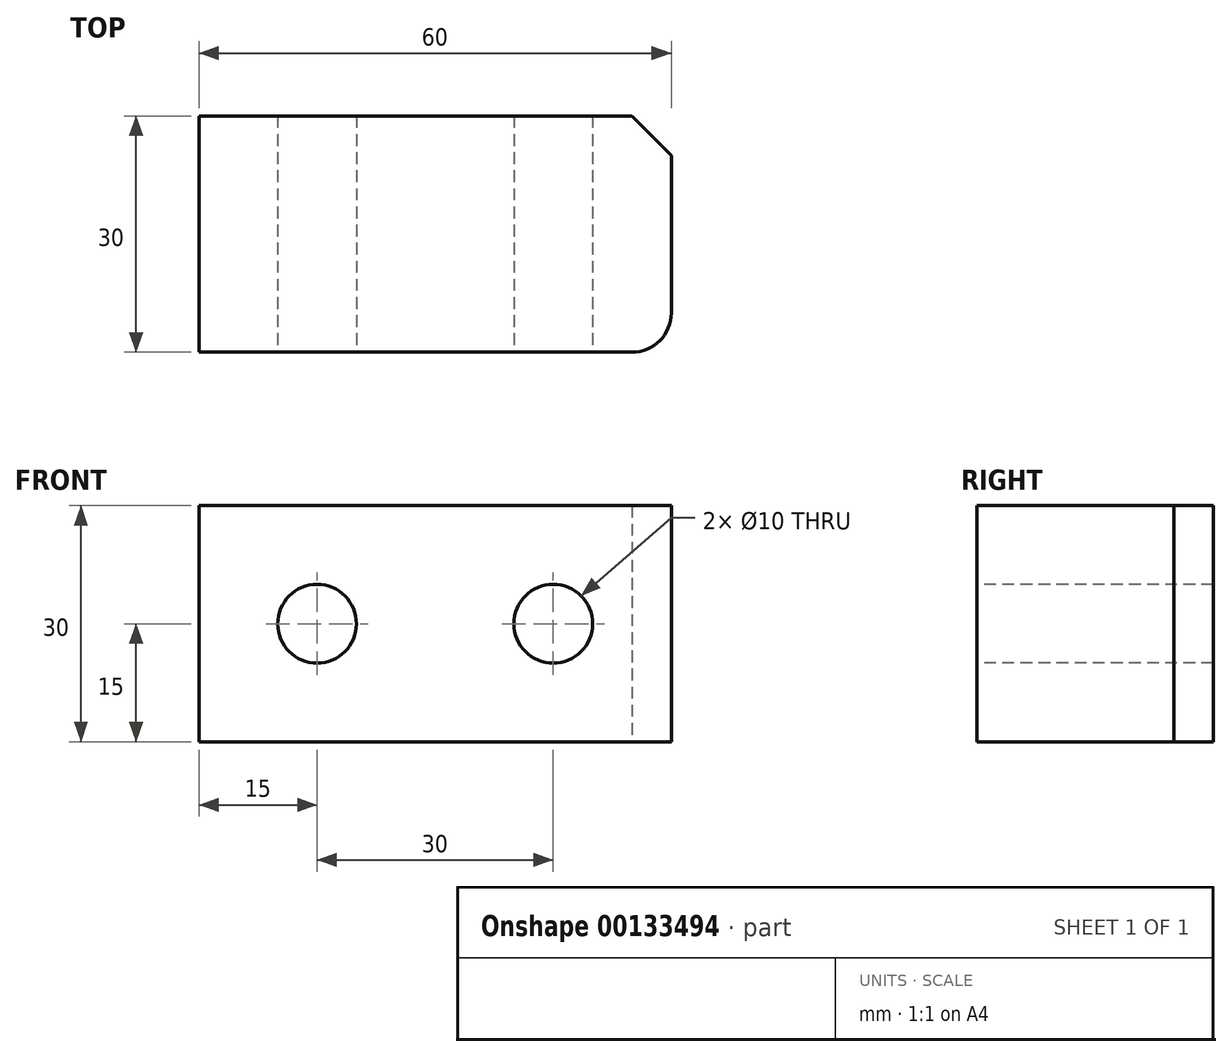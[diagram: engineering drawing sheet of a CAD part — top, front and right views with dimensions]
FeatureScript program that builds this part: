
annotation { "Feature Type Name" : "Feature", "Feature Type Description" : "" }
export const myFeature = defineFeature(function(context is Context, id is Id, definition is map)
    precondition{}
    {
        {
            var Q0;
            Q0=qCreatedBy(makeId("Top.planeOp"),FACE);
            var sketch = newSketch(context, id + "F0", { "sketchPlane" : qUnion([Q0])});
            skLineSegment(sketch, "E0.bottom", {"start": v(-15, 15) * mm, "end": v(15, 15) * mm});
            skLineSegment(sketch, "E0.top", {"start": v(-15, -15) * mm, "end": v(15, -15) * mm});
            skLineSegment(sketch, "E0.left", {"start": v(-15, 15) * mm, "end": v(-15, -15) * mm});
            skLineSegment(sketch, "E0.right", {"start": v(15, 15) * mm, "end": v(15, -15) * mm});
            skPoint(sketch, "E0.middle", {"position": v(0, 0) * mm});
            skSolve(sketch);
        }
        {
            var Q0;
            Q0 = qSketchRegion(id + "F0", true);
            extrude(context, id + "F1", {"entities" : qUnion([Q0]), "depth" : 30 * mm});
        }
        {
            var Q0;
            Q0=makeQuery(id+"F1.opExtrude","SWEPT_FACE",FACE,{"disambiguationData":[OSD([sQuery(id+"F0.wireOp",EDGE,"E0.top")])]});
            var sketch = newSketch(context, id + "F2", { "sketchPlane" : qUnion([Q0])});
            skLineSegment(sketch, "E1", {"start": v(0, 30) * mm, "end": v(0, 15) * mm});
            skPoint(sketch, "E1.endSnap0", {"position": v(0, 30) * mm});
            skCircle(sketch, "E2", {"center": v(0, 15) * mm, "radius": 5 * mm});
            skSolve(sketch);
        }
        {
            var Q0;
            Q0 = qSketchRegion(id + "F2", true);
            extrude(context, id + "F3", {"entities" : qUnion([Q0]), "operationType" : NewBodyOperationType.REMOVE, "endBound" : BoundingType.THROUGH_ALL, "oppositeDirection" : true, "depth" : 25 * mm});
        }
        {
            var Q0;
            Q0=makeQuery(id+"F1.opExtrude","SWEPT_BODY",BODY,{"disambiguationData":[OSD([sQuery(id+"F0.wireOp",EDGE,"E0.bottom"),sQuery(id+"F0.wireOp",EDGE,"E0.top"),sQuery(id+"F0.wireOp",EDGE,"E0.left"),sQuery(id+"F0.wireOp",EDGE,"E0.right")])]});
            var Q1;
            Q1=makeQuery(id+"F1.opExtrude","SWEPT_FACE",FACE,{"disambiguationData":[OSD([sQuery(id+"F0.wireOp",EDGE,"E0.right")])]});
            mirror(context, id + "F4", {"operationType" : NewBodyOperationType.ADD, "entities" : qUnion([Q0]), "mirrorPlane" : qUnion([Q1])});
        }
        {
            var Q0;
            Q0=makeQuery(id+"F4.opPattern","COPY",EDGE,{"derivedFrom":makeQuery(id+"F1.opExtrude","SWEPT_EDGE",EDGE,{"disambiguationData":[OSD([sQuery(id+"F0.wireOp",EDGE,"E0.top"),sQuery(id+"F0.wireOp",EDGE,"E0.left")])]}),"instanceName":"1"});
            fillet(context, id + "F5", {"entities" : qUnion([Q0]), "radius" : 5 * mm, "tangentPropagation" : true, "allowEdgeOverflow" : false});
        }
        {
            var Q0;
            Q0=makeQuery(id+"F4.opPattern","COPY",EDGE,{"derivedFrom":makeQuery(id+"F1.opExtrude","SWEPT_EDGE",EDGE,{"disambiguationData":[OSD([sQuery(id+"F0.wireOp",EDGE,"E0.bottom"),sQuery(id+"F0.wireOp",EDGE,"E0.left")])]}),"instanceName":"1"});
            chamfer(context, id + "F6", {"entities" : qUnion([Q0]), "width" : 5 * mm, "tangentPropagation" : true});
        }
    });
